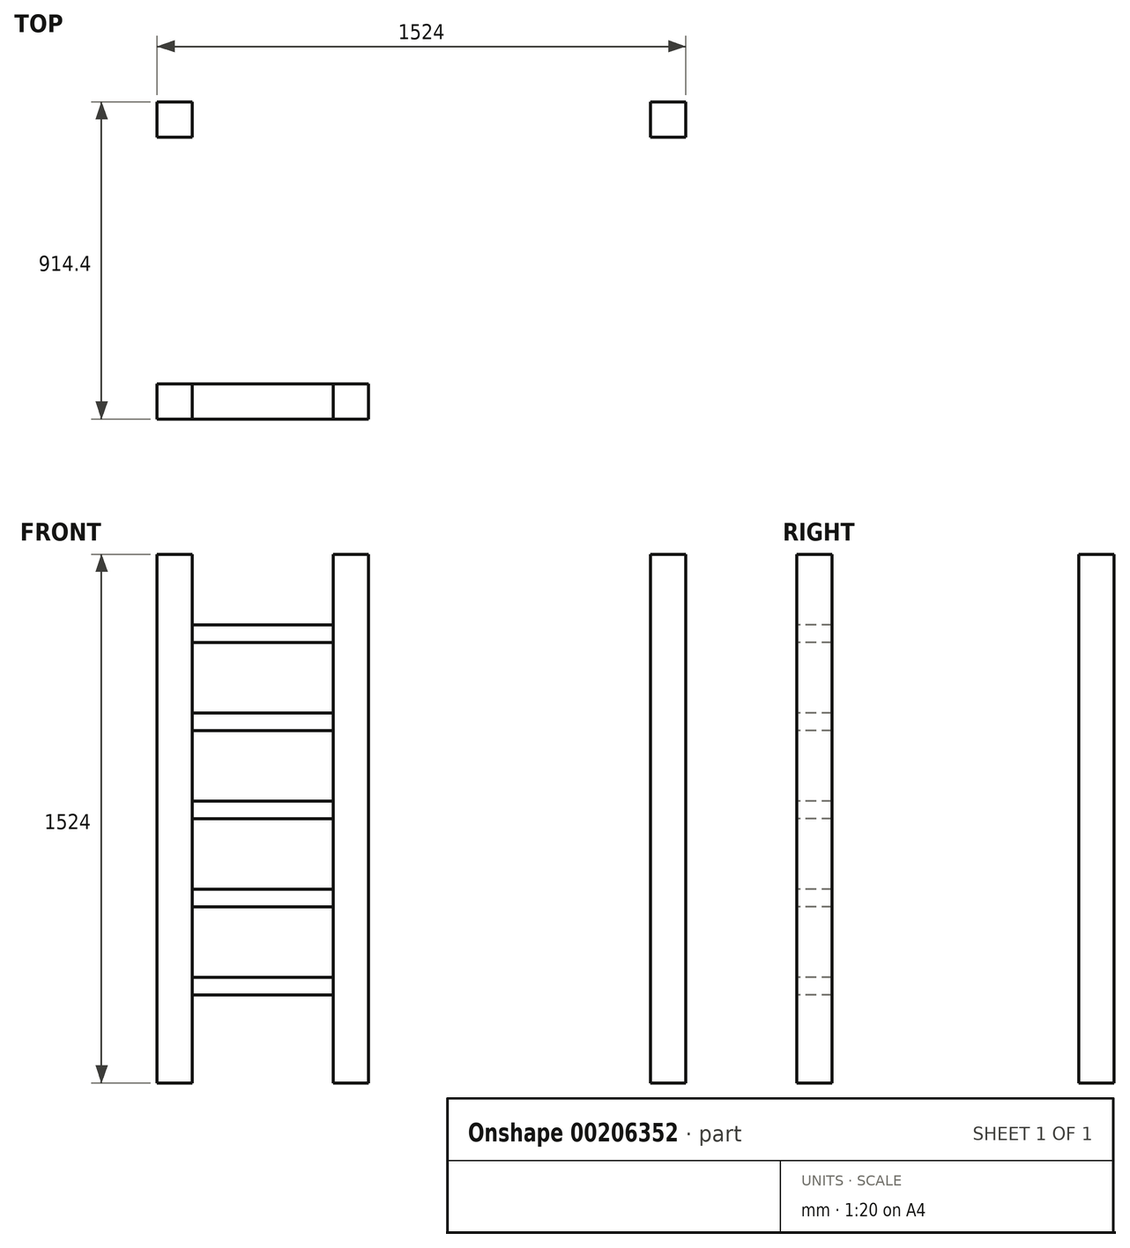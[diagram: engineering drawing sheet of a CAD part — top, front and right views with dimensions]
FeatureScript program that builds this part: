
annotation { "Feature Type Name" : "Feature", "Feature Type Description" : "" }
export const myFeature = defineFeature(function(context is Context, id is Id, definition is map)
    precondition{}
    {
        {
            var Q0;
            Q0=qCreatedBy(makeId("Top.planeOp"),FACE);
            var sketch = newSketch(context, id + "F0", { "sketchPlane" : qUnion([Q0])});
            skLineSegment(sketch, "E0.bottom", {"start": v(-139.56, 56.82) * mm, "end": v(-37.96, 56.82) * mm});
            skLineSegment(sketch, "E0.top", {"start": v(-139.56, -44.78) * mm, "end": v(-37.96, -44.78) * mm});
            skLineSegment(sketch, "E0.left", {"start": v(-139.56, 56.82) * mm, "end": v(-139.56, -44.78) * mm});
            skLineSegment(sketch, "E0.right", {"start": v(-37.96, 56.82) * mm, "end": v(-37.96, -44.78) * mm});
            skSolve(sketch);
        }
        {
            var Q0;
            Q0 = qSketchRegion(id + "F0", true);
            extrude(context, id + "F1", {"entities" : qUnion([Q0]), "depth" : 1524 * mm});
        }
        {
            var Q0;
            Q0=makeQuery(id+"F1.opExtrude","CAP_FACE",FACE,{"disambiguationData":[OSD([sQuery(id+"F0.wireOp",EDGE,"E0.bottom"),sQuery(id+"F0.wireOp",EDGE,"E0.top"),sQuery(id+"F0.wireOp",EDGE,"E0.left"),sQuery(id+"F0.wireOp",EDGE,"E0.right")])],"isStart":true});
            var sketch = newSketch(context, id + "F2", { "sketchPlane" : qUnion([Q0])});
            skLineSegment(sketch, "E1.0", {"start": v(-139.56, -56.82) * mm, "end": v(-37.96, -56.82) * mm});
            skLineSegment(sketch, "E2", {"start": v(-139.56, -56.82) * mm, "end": v(-139.56, 857.58) * mm});
            skLineSegment(sketch, "E3.bottom", {"start": v(-139.56, 857.58) * mm, "end": v(-37.96, 857.58) * mm});
            skLineSegment(sketch, "E3.top", {"start": v(-139.56, 755.98) * mm, "end": v(-37.96, 755.98) * mm});
            skLineSegment(sketch, "E3.left", {"start": v(-139.56, 857.58) * mm, "end": v(-139.56, 755.98) * mm});
            skLineSegment(sketch, "E3.right", {"start": v(-37.96, 857.58) * mm, "end": v(-37.96, 755.98) * mm});
            skSolve(sketch);
        }
        {
            var Q0;
            Q0 = qSketchRegion(id + "F2", true);
            extrude(context, id + "F3", {"entities" : qUnion([Q0]), "oppositeDirection" : true, "depth" : 1524 * mm});
        }
        {
            var Q0;
            Q0=makeQuery(id+"F3.opExtrude","CAP_FACE",FACE,{"disambiguationData":[OSD([sQuery(id+"F2.wireOp",EDGE,"E3.bottom"),sQuery(id+"F2.wireOp",EDGE,"E3.top"),sQuery(id+"F2.wireOp",EDGE,"E3.left"),sQuery(id+"F2.wireOp",EDGE,"E3.right")])],"isStart":true});
            var sketch = newSketch(context, id + "F4", { "sketchPlane" : qUnion([Q0])});
            skLineSegment(sketch, "E4.0", {"start": v(-139.56, 857.58) * mm, "end": v(-37.96, 857.58) * mm});
            skLineSegment(sketch, "E5", {"start": v(-139.56, 857.58) * mm, "end": v(470.04, 857.58) * mm});
            skLineSegment(sketch, "E6.bottom", {"start": v(470.04, 857.58) * mm, "end": v(368.44, 857.58) * mm});
            skLineSegment(sketch, "E6.top", {"start": v(470.04, 755.98) * mm, "end": v(368.44, 755.98) * mm});
            skLineSegment(sketch, "E6.left", {"start": v(470.04, 857.58) * mm, "end": v(470.04, 755.98) * mm});
            skLineSegment(sketch, "E6.right", {"start": v(368.44, 857.58) * mm, "end": v(368.44, 755.98) * mm});
            skSolve(sketch);
        }
        {
            var Q0;
            Q0 = qSketchRegion(id + "F4", true);
            extrude(context, id + "F5", {"entities" : qUnion([Q0]), "oppositeDirection" : true, "depth" : 1524 * mm});
        }
        {
            var Q0;
            Q0=makeQuery(id+"F3.opExtrude","SWEPT_FACE",FACE,{"disambiguationData":[OSD([sQuery(id+"F2.wireOp",EDGE,"E3.right")])]});
            var sketch = newSketch(context, id + "F6", { "sketchPlane" : qUnion([Q0])});
            skLineSegment(sketch, "E7.bottom", {"start": v(-857.58, 254) * mm, "end": v(-755.98, 254) * mm});
            skLineSegment(sketch, "E7.top", {"start": v(-857.58, 304.8) * mm, "end": v(-755.98, 304.8) * mm});
            skLineSegment(sketch, "E7.left", {"start": v(-857.58, 254) * mm, "end": v(-857.58, 304.8) * mm});
            skLineSegment(sketch, "E7.right", {"start": v(-755.98, 254) * mm, "end": v(-755.98, 304.8) * mm});
            skLineSegment(sketch, "E8.0.1.0", {"start": v(-857.58, 558.8) * mm, "end": v(-755.98, 558.8) * mm});
            skLineSegment(sketch, "E8.0.1.1", {"start": v(-857.58, 508) * mm, "end": v(-857.58, 558.8) * mm});
            skLineSegment(sketch, "E8.0.1.2", {"start": v(-755.98, 508) * mm, "end": v(-755.98, 558.8) * mm});
            skLineSegment(sketch, "E8.0.1.3", {"start": v(-857.58, 508) * mm, "end": v(-755.98, 508) * mm});
            skLineSegment(sketch, "E8.0.2.0", {"start": v(-857.58, 812.8) * mm, "end": v(-755.98, 812.8) * mm});
            skLineSegment(sketch, "E8.0.2.1", {"start": v(-857.58, 762) * mm, "end": v(-857.58, 812.8) * mm});
            skLineSegment(sketch, "E8.0.2.2", {"start": v(-755.98, 762) * mm, "end": v(-755.98, 812.8) * mm});
            skLineSegment(sketch, "E8.0.2.3", {"start": v(-857.58, 762) * mm, "end": v(-755.98, 762) * mm});
            skLineSegment(sketch, "E8.0.3.0", {"start": v(-857.58, 1066.8) * mm, "end": v(-755.98, 1066.8) * mm});
            skLineSegment(sketch, "E8.0.3.1", {"start": v(-857.58, 1016) * mm, "end": v(-857.58, 1066.8) * mm});
            skLineSegment(sketch, "E8.0.3.2", {"start": v(-755.98, 1016) * mm, "end": v(-755.98, 1066.8) * mm});
            skLineSegment(sketch, "E8.0.3.3", {"start": v(-857.58, 1016) * mm, "end": v(-755.98, 1016) * mm});
            skLineSegment(sketch, "E8.0.4.0", {"start": v(-857.58, 1320.8) * mm, "end": v(-755.98, 1320.8) * mm});
            skLineSegment(sketch, "E8.0.4.1", {"start": v(-857.58, 1270) * mm, "end": v(-857.58, 1320.8) * mm});
            skLineSegment(sketch, "E8.0.4.2", {"start": v(-755.98, 1270) * mm, "end": v(-755.98, 1320.8) * mm});
            skLineSegment(sketch, "E8.0.4.3", {"start": v(-857.58, 1270) * mm, "end": v(-755.98, 1270) * mm});
            skLineSegment(sketch, "E8.direction1", {"start": v(-857.58, 304.8) * mm, "end": v(-832.18, 304.8) * mm, "construction": true});
            skLineSegment(sketch, "E8.direction2", {"start": v(-857.58, 304.8) * mm, "end": v(-857.58, 558.8) * mm, "construction": true});
            skSolve(sketch);
        }
        {
            var Q0;
            Q0 = qSketchRegion(id + "F6", true);
            extrude(context, id + "F7", {"entities" : qUnion([Q0]), "endBound" : BoundingType.UP_TO_NEXT, "depth" : 25.4 * mm});
        }
        {
            var Q0;
            Q0=qCreatedBy(makeId("Top.planeOp"),FACE);
            var sketch = newSketch(context, id + "F8", { "sketchPlane" : qUnion([Q0])});
            skLineSegment(sketch, "E9.0", {"start": v(-139.56, 56.82) * mm, "end": v(-37.96, 56.82) * mm});
            skLineSegment(sketch, "E10", {"start": v(-139.56, 56.82) * mm, "end": v(1384.44, 56.82) * mm});
            skLineSegment(sketch, "E11.bottom", {"start": v(1384.44, 56.82) * mm, "end": v(1282.84, 56.82) * mm});
            skLineSegment(sketch, "E11.top", {"start": v(1384.44, -44.78) * mm, "end": v(1282.84, -44.78) * mm});
            skLineSegment(sketch, "E11.left", {"start": v(1384.44, 56.82) * mm, "end": v(1384.44, -44.78) * mm});
            skLineSegment(sketch, "E11.right", {"start": v(1282.84, 56.82) * mm, "end": v(1282.84, -44.78) * mm});
            skSolve(sketch);
        }
        {
            var Q0;
            Q0 = qSketchRegion(id + "F8", true);
            extrude(context, id + "F9", {"entities" : qUnion([Q0]), "depth" : 1524 * mm});
        }
    });
